# Revit family: Sanitary_Basins_Sanindusa_Flux-Wall-Hung-Washbasin
name_source: partatom
category: Plumbing Fixtures
revit_build: Autodesk Revit 2018 (Build: 20170223_1515(x64)
units: mm (PartAtom-declared; Revit-internal decimal feet)

## family parameters
Always vertical = Yes
Cut with Voids When Loaded = No
OmniClass Number = 23.45.00.00
OmniClass Title = Sanitary, Laundry, and Cleaning Equipment
Part Type = Normal
Room Calculation Point = No
Round Connector Dimension = Use Diameter
Shared = No
Work Plane-Based = Yes

## types (1)
- Sanitary_Basins_Sanindusa_Flux-Wall-Hung-Washbasin
    AssetType = Fixed
    Category = Pr_40_20_96_18: Counter top wash basins
    CodePerformance = EN 14688:2015 CL 00
    Color = white
    Constituents = Fixing kit included;  Siphon adapter ref. 4V9811 included.
    Cost = 0 $
    Default Elevation = 1219 mm
    Description = Waste water appliance for washing the upper parts of the body.
    DrainSize = 44 mm  [stored 0.144357 ft]
    Edition number = 1
    Features = Installation wall-mounted. Glazed on all sides. Not rectified. Not compatible with valves. Without overflow.
    Finish = gloss
    Installation Instructions = https://www.tec.sanindusa.pt
    InstallationDate = 1900-12-31T23:59:59
    ManufacturerName = Sanindusa
    ManufacturerURL = www.tec.sanindusa.pt
    Material = vitreous china
    ModelNumber = 109750004
    ModelReference = Flux
    Name = 65x39 flux Washbasin
    NominalHeight = 95 mm
    NominalLength = 655 mm  [stored 2.14895 ft]
    NominalWidth = 390 mm  [stored 1.27953 ft]
    Product Guid = 28a524d6-ce4a-47db-b757-68e8be3664ca
    Product data url = https://bimobject.com
    ProductInformation = https://www.tec.sanindusa.pt
    ProductionYear = 2018
    Shape = rectangular
    Size = 655x390x95
    SpilloverLevel = 0 mm  [stored 0 ft]
    URL = www.tec.sanindusa.pt
    Uniclass2015Code = Pr_40_20_96_18
    Uniclass2015Title = Counter top wash basins
    Uniclass2015Version = Products v1.6
    Version = 1
    WarrantyDescription = https://www.tec.sanindusa.pt
    WarrantyDurationParts = 5
    WarrantyDurationUnit = year
    WarrantyStartDate = 1900-12-31T23:59:59
1900-12-31T23:59:59
    WashHandBasinMounting = wallhung
    WashHandBasinType = handrinse
    Weight = 13.00 kg

note: [stored X ft] marks values corroborated as IEEE doubles in the binary element streams (Revit-internal decimal feet)

## geometry (parser evidence)
native form markers: Sweep x8
no freeform markers — native parametric forms only
